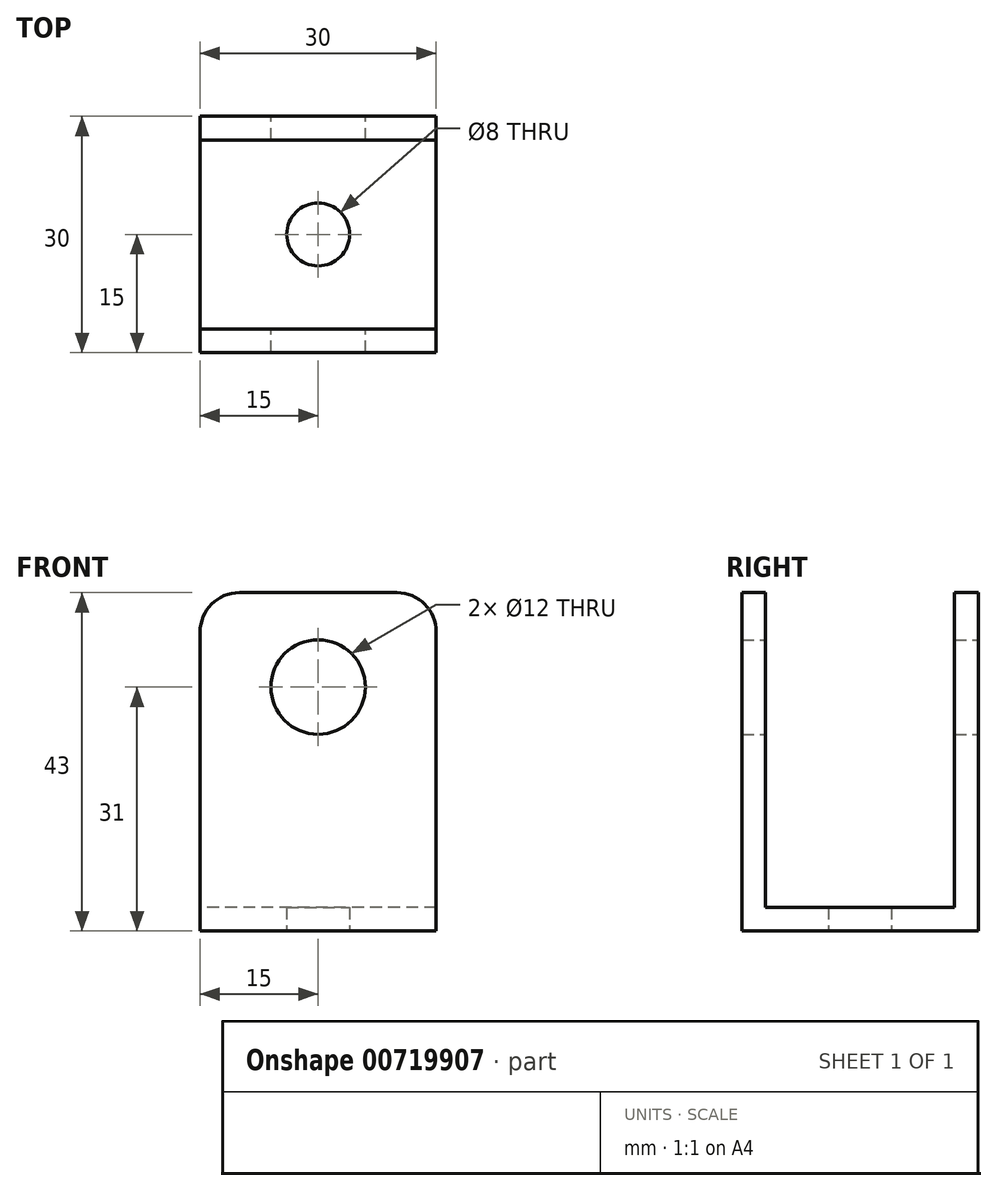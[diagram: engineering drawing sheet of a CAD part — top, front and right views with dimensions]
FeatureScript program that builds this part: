
annotation { "Feature Type Name" : "Feature", "Feature Type Description" : "" }
export const myFeature = defineFeature(function(context is Context, id is Id, definition is map)
    precondition{}
    {
        {
            var Q0;
            Q0=qCreatedBy(makeId("Right.planeOp"),FACE);
            var sketch = newSketch(context, id + "F0", { "sketchPlane" : qUnion([Q0])});
            skLineSegment(sketch, "E0", {"start": v(-15, 40) * mm, "end": v(-15, -3) * mm});
            skLineSegment(sketch, "E1", {"start": v(-15, -3) * mm, "end": v(15, -3) * mm});
            skLineSegment(sketch, "E2", {"start": v(15, -3) * mm, "end": v(15, 40) * mm});
            skLineSegment(sketch, "E3", {"start": v(15, 40) * mm, "end": v(12, 40) * mm});
            skLineSegment(sketch, "E4", {"start": v(12, 40) * mm, "end": v(12, 0) * mm});
            skLineSegment(sketch, "E5", {"start": v(12, 0) * mm, "end": v(-12, 0) * mm});
            skLineSegment(sketch, "E6", {"start": v(-12, 0) * mm, "end": v(-12, 40) * mm});
            skLineSegment(sketch, "E7", {"start": v(-12, 40) * mm, "end": v(-15, 40) * mm});
            skSolve(sketch);
        }
        {
            var Q0;
            Q0=qSketchRegion(id+"F0",true);
            extrude(context, id + "F1", {"entities" : qUnion([Q0]), "depth" : 30 * mm});
        }
        {
            var Q0;
            Q0=makeQuery(id+"F1.opExtrude","SWEPT_FACE",FACE,{"disambiguationData":[OSD([sQuery(id+"F0.wireOp",EDGE,"E2")])]});
            var sketch = newSketch(context, id + "F2", { "sketchPlane" : qUnion([Q0])});
            skCircle(sketch, "E8", {"center": v(-15, 28) * mm, "radius": 6 * mm});
            skLineSegment(sketch, "E9", {"start": v(-15, 40) * mm, "end": v(-15, -3) * mm});
            skSolve(sketch);
        }
        {
            var Q0;
            Q0=qSketchRegion(id+"F2",true);
            extrude(context, id + "F3", {"entities" : qUnion([Q0]), "operationType" : NewBodyOperationType.REMOVE, "endBound" : BoundingType.THROUGH_ALL, "oppositeDirection" : true, "depth" : 25 * mm});
        }
        {
            var Q0;
            Q0=makeQuery(id+"F1.opExtrude","CAP_EDGE",EDGE,{"disambiguationData":[OSD([sQuery(id+"F0.wireOp",EDGE,"E3")])],"isStart":true});
            var Q1;
            Q1=makeQuery(id+"F1.opExtrude","CAP_EDGE",EDGE,{"disambiguationData":[OSD([sQuery(id+"F0.wireOp",EDGE,"E7")])],"isStart":true});
            var Q2;
            Q2=makeQuery(id+"F1.opExtrude","CAP_EDGE",EDGE,{"disambiguationData":[OSD([sQuery(id+"F0.wireOp",EDGE,"E3")])],"isStart":false});
            var Q3;
            Q3=makeQuery(id+"F1.opExtrude","CAP_EDGE",EDGE,{"disambiguationData":[OSD([sQuery(id+"F0.wireOp",EDGE,"E7")])],"isStart":false});
            fillet(context, id + "F4", {"entities" : qUnion([Q0, Q1, Q2, Q3]), "radius" : 5 * mm, "tangentPropagation" : true, "allowEdgeOverflow" : false});
        }
        {
            var Q0;
            Q0=makeQuery(id+"F1.opExtrude","SWEPT_FACE",FACE,{"disambiguationData":[OSD([sQuery(id+"F0.wireOp",EDGE,"E1")])]});
            var sketch = newSketch(context, id + "F5", { "sketchPlane" : qUnion([Q0])});
            skCircle(sketch, "E10", {"center": v(15, 0) * mm, "radius": 4 * mm});
            skLineSegment(sketch, "E11", {"start": v(15, 15) * mm, "end": v(15, -15) * mm, "construction": true});
            skSolve(sketch);
        }
        {
            var Q0;
            Q0 = qSketchRegion(id + "F5", true);
            extrude(context, id + "F6", {"entities" : qUnion([Q0]), "operationType" : NewBodyOperationType.REMOVE, "endBound" : BoundingType.THROUGH_ALL, "oppositeDirection" : true, "depth" : 25 * mm, "offsetDistance" : 25 * mm});
        }
    });
